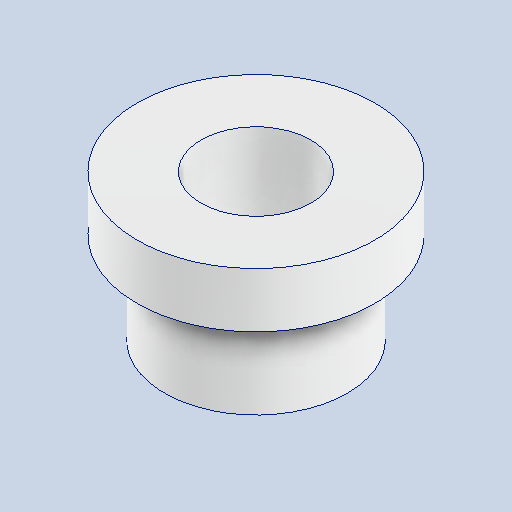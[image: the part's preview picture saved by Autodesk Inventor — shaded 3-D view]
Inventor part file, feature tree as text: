
AUTODESK INVENTOR PART (.ipt)
format: ipt  version: 2025.1 (Build 291241000, 241)  size: 229,888 bytes
history: native  units: mm
features: sketch x2, revolve x1, hole x1
ambient origin geometry x8: Origin, YZ Plane, XZ Plane, XY Plane, X Axis, Y Axis, Z Axis, Center Point
bodies: Volumenkörper1 (feature_tree)
feature tree (4):
  revolve  "Umdrehung1"
  hole  "Bohrung1"  [1 undecoded]
  sketch  "Skizze1"  dims[d0=3.0mm d1=5.0mm]
  sketch  "Skizze2"  dims[d2=10.0mm d3=13.0mm d4=90.0deg d5=6.0mm d6=6.0mm d7=4.0mm d8=2.0mm d9=90.0deg d10=8.0mm d11=20.594885mm]
note: 1 required parameter value undecoded (feature->parameter linkage not recoverable at this tier; creation-order binding heuristic only, values carry confidence <= 0.55)
